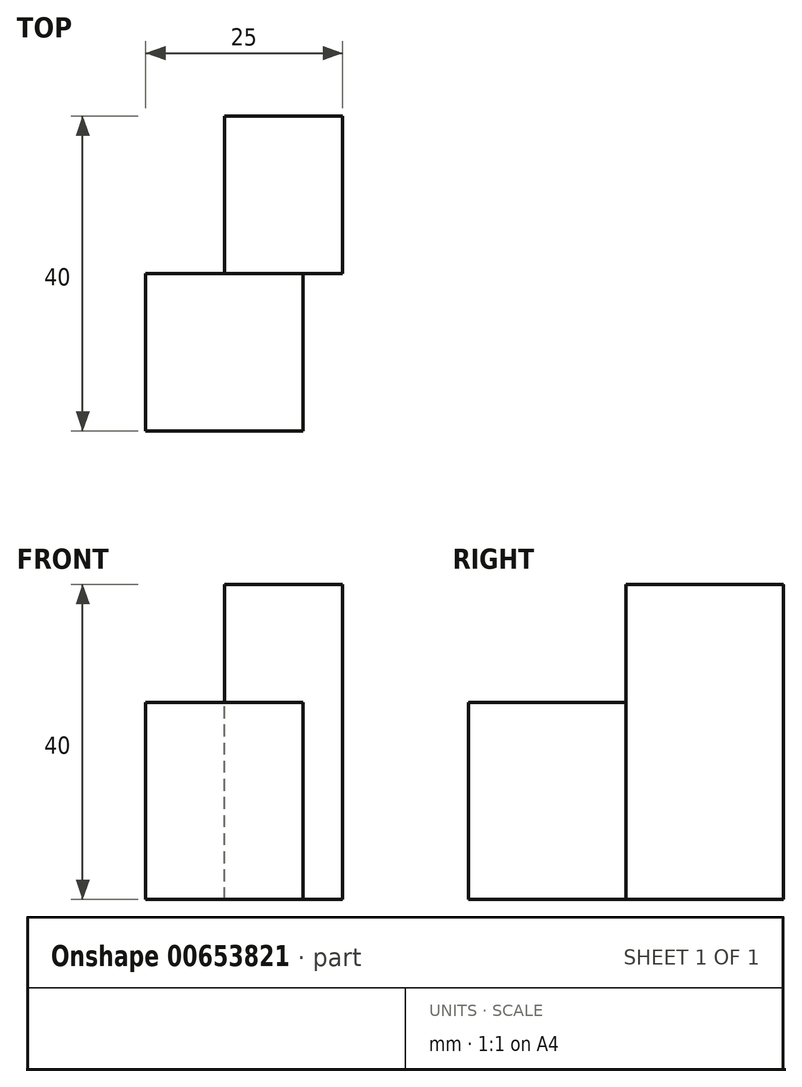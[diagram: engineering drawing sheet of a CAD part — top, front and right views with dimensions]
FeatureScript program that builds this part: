
annotation { "Feature Type Name" : "Feature", "Feature Type Description" : "" }
export const myFeature = defineFeature(function(context is Context, id is Id, definition is map)
    precondition{}
    {
        {
            var Q0;
            Q0=qCreatedBy(makeId("Front.planeOp"),FACE);
            var sketch = newSketch(context, id + "F0", { "sketchPlane" : qUnion([Q0])});
            skLineSegment(sketch, "E0.bottom", {"start": v(-10, 12.5) * mm, "end": v(10, 12.5) * mm});
            skLineSegment(sketch, "E0.top", {"start": v(-10, -12.5) * mm, "end": v(10, -12.5) * mm});
            skLineSegment(sketch, "E0.left", {"start": v(-10, 12.5) * mm, "end": v(-10, -12.5) * mm});
            skLineSegment(sketch, "E0.right", {"start": v(10, 12.5) * mm, "end": v(10, -12.5) * mm});
            skPoint(sketch, "E0.middle", {"position": v(0, 0) * mm});
            skSolve(sketch);
        }
        {
            var Q0;
            Q0=makeQuery(id+"F0.imprint","IMPRINT",FACE,{"disambiguationData":[TD([[makeQuery(id+"F0.imprint","IMPRINT",EDGE,{"derivedFrom":sQuery(id+"F0.wireOp",EDGE,"E0.bottom")}),-1.0]])]});
            extrude(context, id + "F1", {"entities" : qUnion([Q0]), "depth" : 20 * mm, "offsetDistance" : 25.4 * mm});
        }
        {
            var Q0;
            Q0=qCreatedBy(makeId("Right.planeOp"),FACE);
            var sketch = newSketch(context, id + "F2", { "sketchPlane" : qUnion([Q0])});
            skLineSegment(sketch, "E1.bottom", {"start": v(0, -12.5) * mm, "end": v(20, -12.5) * mm});
            skLineSegment(sketch, "E1.top", {"start": v(0, 27.5) * mm, "end": v(20, 27.5) * mm});
            skLineSegment(sketch, "E1.left", {"start": v(0, -12.5) * mm, "end": v(0, 27.5) * mm});
            skLineSegment(sketch, "E1.right", {"start": v(20, -12.5) * mm, "end": v(20, 27.5) * mm});
            skSolve(sketch);
        }
        {
            var Q0;
            Q0=makeQuery(id+"F2.imprint","IMPRINT",FACE,{"disambiguationData":[TD([[makeQuery(id+"F2.imprint","IMPRINT",EDGE,{"derivedFrom":sQuery(id+"F2.wireOp",EDGE,"E1.bottom")}),1.0]])]});
            extrude(context, id + "F3", {"entities" : qUnion([Q0]), "depth" : 15 * mm, "offsetDistance" : 25.4 * mm});
        }
    });
